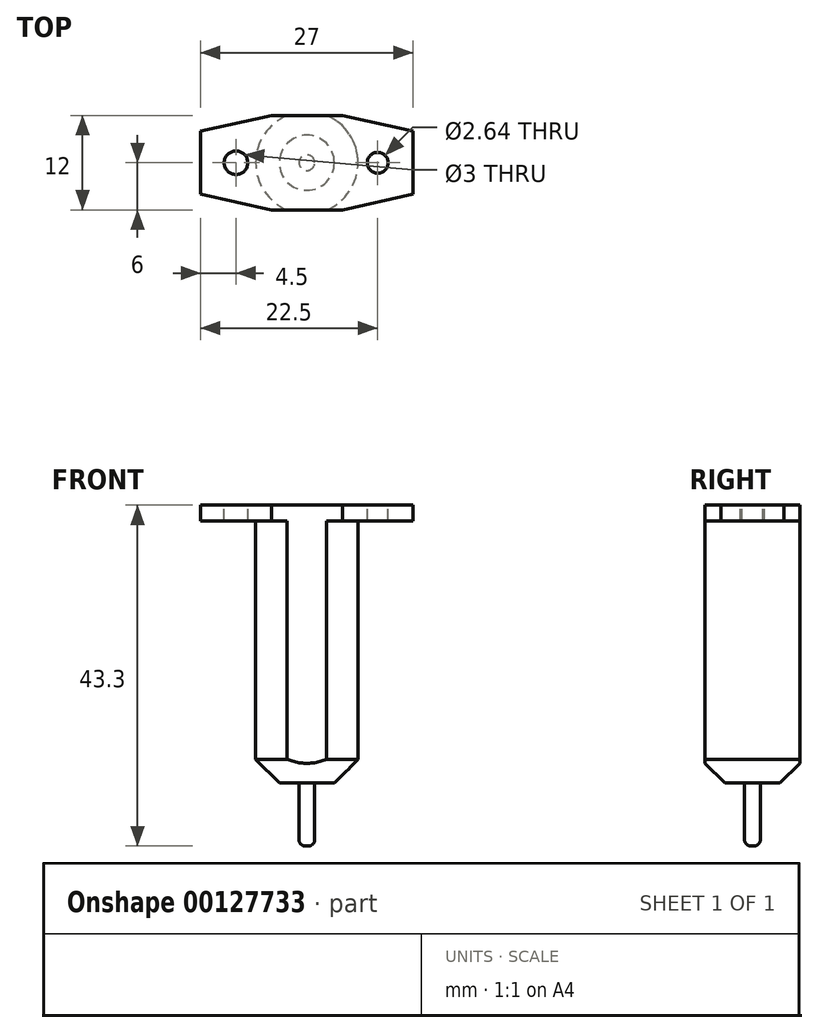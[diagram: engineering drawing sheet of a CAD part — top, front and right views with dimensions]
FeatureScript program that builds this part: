
annotation { "Feature Type Name" : "Feature", "Feature Type Description" : "" }
export const myFeature = defineFeature(function(context is Context, id is Id, definition is map)
    precondition{}
    {
        {
            var Q0;
            Q0=qCreatedBy(makeId("Top.planeOp"),FACE);
            var sketch = newSketch(context, id + "F0", { "sketchPlane" : qUnion([Q0])});
            skCircle(sketch, "E0", {"center": v(0, 0) * mm, "radius": 6.5 * mm});
            skSolve(sketch);
        }
        {
            var Q0;
            Q0 = qSketchRegion(id + "F0", true);
            extrude(context, id + "F1", {"entities" : qUnion([Q0]), "depth" : 33.3 * mm});
        }
        {
            var Q0;
            Q0=makeQuery(id+"F1.opExtrude","CAP_EDGE",EDGE,{"disambiguationData":[OSD([sQuery(id+"F0.wireOp",EDGE,"E0")])],"isStart":true});
            chamfer(context, id + "F2", {"entities" : qUnion([Q0]), "width" : 3 * mm, "tangentPropagation" : true});
        }
        {
            var Q0;
            Q0=makeQuery(id+"F1.opExtrude","CAP_FACE",FACE,{"disambiguationData":[OSD([sQuery(id+"F0.wireOp",EDGE,"E0")])],"isStart":false});
            var sketch = newSketch(context, id + "F3", { "sketchPlane" : qUnion([Q0])});
            skLineSegment(sketch, "E1.bottom", {"start": v(-13.5, 6) * mm, "end": v(13.5, 6) * mm});
            skLineSegment(sketch, "E1.top", {"start": v(-13.5, -6) * mm, "end": v(13.5, -6) * mm});
            skLineSegment(sketch, "E1.left", {"start": v(-13.5, 6) * mm, "end": v(-13.5, -6) * mm});
            skLineSegment(sketch, "E1.right", {"start": v(13.5, 6) * mm, "end": v(13.5, -6) * mm});
            skSolve(sketch);
        }
        {
            var Q0;
            Q0 = qSketchRegion(id + "F3", true);
            extrude(context, id + "F4", {"entities" : qUnion([Q0]), "operationType" : NewBodyOperationType.ADD, "depth" : 2 * mm});
        }
        {
            var Q0;
            Q0=makeQuery(id+"F1.opExtrude","CAP_FACE",FACE,{"disambiguationData":[OSD([sQuery(id+"F0.wireOp",EDGE,"E0")])],"isStart":true});
            var sketch = newSketch(context, id + "F5", { "sketchPlane" : qUnion([Q0])});
            skCircle(sketch, "E2", {"center": v(0, 0) * mm, "radius": 1 * mm});
            skSolve(sketch);
        }
        {
            var Q0;
            Q0 = qSketchRegion(id + "F5", true);
            extrude(context, id + "F6", {"entities" : qUnion([Q0]), "operationType" : NewBodyOperationType.ADD, "depth" : 8 * mm});
        }
        {
            var Q0;
            Q0=makeQuery(id+"F6.opExtrude","CAP_EDGE",EDGE,{"disambiguationData":[OSD([sQuery(id+"F5.wireOp",EDGE,"E2")])],"isStart":false});
            fillet(context, id + "F7", {"entities" : qUnion([Q0]), "radius" : .8 * mm, "tangentPropagation" : true, "allowEdgeOverflow" : false});
        }
        {
            var Q0;
            Q0=makeQuery(id+"F4.opExtrude","CAP_FACE",FACE,{"disambiguationData":[OSD([sQuery(id+"F3.wireOp",EDGE,"E1.bottom"),sQuery(id+"F3.wireOp",EDGE,"E1.top"),sQuery(id+"F3.wireOp",EDGE,"E1.left"),sQuery(id+"F3.wireOp",EDGE,"E1.right")])],"isStart":false});
            var sketch = newSketch(context, id + "F8", { "sketchPlane" : qUnion([Q0])});
            skCircle(sketch, "E3", {"center": v(-9, 0) * mm, "radius": 1.5 * mm});
            skCircle(sketch, "E4", {"center": v(9, 0) * mm, "radius": 1.32 * mm});
            skSolve(sketch);
        }
        {
            var Q0;
            Q0 = qSketchRegion(id + "F8", true);
            extrude(context, id + "F9", {"entities" : qUnion([Q0]), "operationType" : NewBodyOperationType.REMOVE, "oppositeDirection" : true, "depth" : 25 * mm});
        }
        {
            var Q0;
            Q0=makeQuery(id+"F4.opExtrude","CAP_FACE",FACE,{"disambiguationData":[OSD([sQuery(id+"F3.wireOp",EDGE,"E1.bottom"),sQuery(id+"F3.wireOp",EDGE,"E1.top"),sQuery(id+"F3.wireOp",EDGE,"E1.left"),sQuery(id+"F3.wireOp",EDGE,"E1.right")])],"isStart":false});
            var sketch = newSketch(context, id + "F10", { "sketchPlane" : qUnion([Q0])});
            skLineSegment(sketch, "E5", {"start": v(-13.5, -6) * mm, "end": v(-13.5, -4) * mm});
            skLineSegment(sketch, "E6", {"start": v(-13.5, -4) * mm, "end": v(-4.5, -6) * mm});
            skLineSegment(sketch, "E7", {"start": v(-4.5, -6) * mm, "end": v(-13.5, -6) * mm});
            skLineSegment(sketch, "E8", {"start": v(-13.5, 6) * mm, "end": v(-4.5, 6) * mm});
            skLineSegment(sketch, "E9", {"start": v(-4.5, 6) * mm, "end": v(-13.5, 4) * mm});
            skLineSegment(sketch, "E10", {"start": v(-13.5, 4) * mm, "end": v(-13.5, 6) * mm});
            skLineSegment(sketch, "E11", {"start": v(4.5, -6) * mm, "end": v(13.5, -4) * mm});
            skLineSegment(sketch, "E12", {"start": v(13.5, -4) * mm, "end": v(13.5, -6) * mm});
            skLineSegment(sketch, "E13", {"start": v(13.5, -6) * mm, "end": v(4.5, -6) * mm});
            skLineSegment(sketch, "E14", {"start": v(13.5, 6) * mm, "end": v(13.5, 4) * mm});
            skLineSegment(sketch, "E15", {"start": v(13.5, 4) * mm, "end": v(4.5, 6) * mm});
            skLineSegment(sketch, "E16", {"start": v(4.5, 6) * mm, "end": v(13.5, 6) * mm});
            skSolve(sketch);
        }
        {
            var Q0;
            Q0 = qSketchRegion(id + "F10", true);
            extrude(context, id + "F11", {"entities" : qUnion([Q0]), "operationType" : NewBodyOperationType.REMOVE, "endBound" : BoundingType.UP_TO_NEXT, "oppositeDirection" : true, "depth" : 25 * mm});
        }
        {
            var Q0;
            Q0=makeQuery(id+"F4.opExtrude","SWEPT_FACE",FACE,{"disambiguationData":[OSD([sQuery(id+"F3.wireOp",EDGE,"E1.top")])]});
            var sketch = newSketch(context, id + "F12", { "sketchPlane" : qUnion([Q0])});
            skPoint(sketch, "E17.oppositeSnap0", {"position": v(4.5, 34.3) * mm});
            skLineSegment(sketch, "E17.bottom", {"start": v(-4.5, 35.3) * mm, "end": v(4.5, 35.3) * mm});
            skLineSegment(sketch, "E17.top", {"start": v(-4.5, -9.3) * mm, "end": v(4.5, -9.3) * mm});
            skLineSegment(sketch, "E17.left", {"start": v(-4.5, 35.3) * mm, "end": v(-4.5, -9.3) * mm});
            skLineSegment(sketch, "E17.right", {"start": v(4.5, 35.3) * mm, "end": v(4.5, -9.3) * mm});
            skSolve(sketch);
        }
        {
            var Q0;
            Q0 = qSketchRegion(id + "F12", true);
            extrude(context, id + "F13", {"entities" : qUnion([Q0]), "operationType" : NewBodyOperationType.REMOVE, "depth" : 5 * mm});
        }
        {
            var Q0;
            Q0=makeQuery(id+"F4.opExtrude","SWEPT_FACE",FACE,{"disambiguationData":[OSD([sQuery(id+"F3.wireOp",EDGE,"E1.bottom")])]});
            var sketch = newSketch(context, id + "F14", { "sketchPlane" : qUnion([Q0])});
            skLineSegment(sketch, "E18.bottom", {"start": v(-4.5, 33.3) * mm, "end": v(4.5, 33.3) * mm});
            skLineSegment(sketch, "E18.top", {"start": v(-4.5, -2) * mm, "end": v(4.5, -2) * mm});
            skLineSegment(sketch, "E18.left", {"start": v(-4.5, 33.3) * mm, "end": v(-4.5, -2) * mm});
            skLineSegment(sketch, "E18.right", {"start": v(4.5, 33.3) * mm, "end": v(4.5, -2) * mm});
            skSolve(sketch);
        }
        {
            var Q0;
            Q0 = qSketchRegion(id + "F14", true);
            extrude(context, id + "F15", {"entities" : qUnion([Q0]), "operationType" : NewBodyOperationType.REMOVE, "depth" : 5 * mm});
        }
    });
